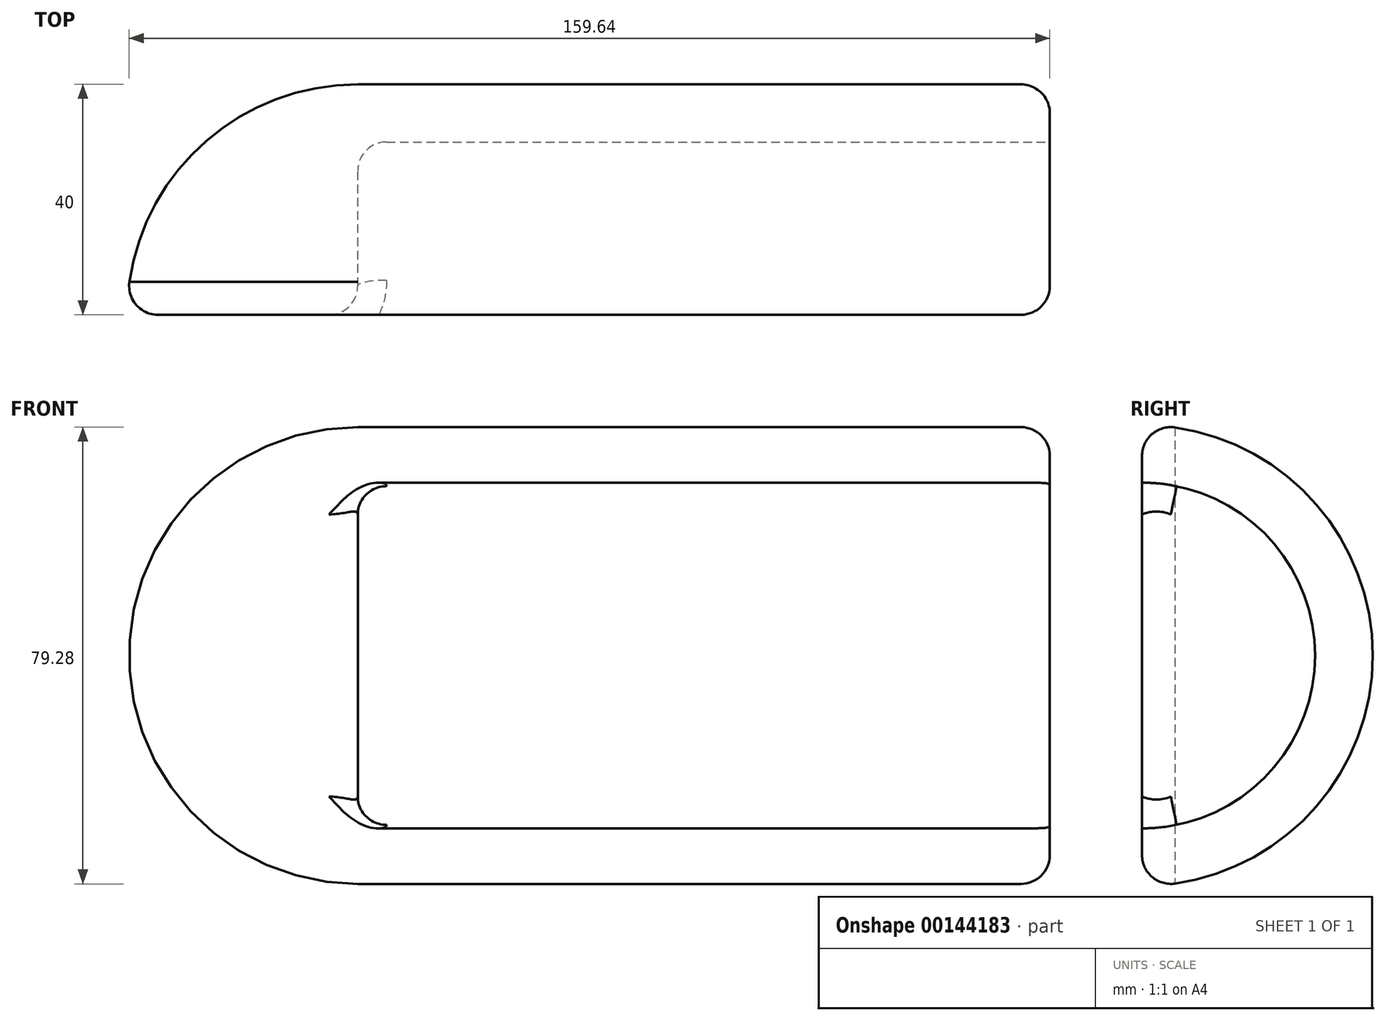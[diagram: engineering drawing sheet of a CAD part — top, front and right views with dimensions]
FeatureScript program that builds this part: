
annotation { "Feature Type Name" : "Feature", "Feature Type Description" : "" }
export const myFeature = defineFeature(function(context is Context, id is Id, definition is map)
    precondition{}
    {
        {
            var Q0;
            Q0=qCreatedBy(makeId("Front.planeOp"),FACE);
            var sketch = newSketch(context, id + "F0", { "sketchPlane" : qUnion([Q0])});
            skLineSegment(sketch, "E0", {"start": v(0, 40) * mm, "end": v(-120, 40) * mm});
            skLineSegment(sketch, "E1", {"start": v(0, 0) * mm, "end": v(-130.73, 0) * mm, "construction": true});
            skArc(sketch, "E2", {"start": v(-120, 40) * mm, "mid": v(-148.28, 28.28) * mm, "end": v(-160, 0) * mm});
            skLineSegment(sketch, "E3", {"start": v(-160, 0) * mm, "end": v(0, 0) * mm});
            skLineSegment(sketch, "E4", {"start": v(0, 40) * mm, "end": v(0, 0) * mm});
            skSolve(sketch);
        }
        {
            var Q0;
            Q0=makeQuery(id+"F0.imprint","IMPRINT",FACE,{"disambiguationData":[TD([[makeQuery(id+"F0.imprint","IMPRINT",EDGE,{"derivedFrom":sQuery(id+"F0.wireOp",EDGE,"E0")}),1.0]])]});
            var Q1;
            Q1=sQuery(id+"F0.wireOp",EDGE,"E1");
            revolve(context, id + "F1", {"entities" : qUnion([Q0]), "axis" : qUnion([Q1]), "revolveType" : RevolveType.FULL});
        }
        {
            var Q0;
            Q0=makeQuery(id+"F1.opRevolve","SWEPT_FACE",FACE,{"disambiguationData":[OSD([sQuery(id+"F0.wireOp",EDGE,"E4")])]});
            var sketch = newSketch(context, id + "F2", { "sketchPlane" : qUnion([Q0])});
            skCircle(sketch, "E5", {"center": v(0, 0) * mm, "radius": 30 * mm});
            skSolve(sketch);
        }
        {
            var Q0;
            Q0=makeQuery(id+"F2.imprint","IMPRINT",FACE,{"disambiguationData":[TD([[makeQuery(id+"F2.imprint","IMPRINT",EDGE,{"derivedFrom":sQuery(id+"F2.wireOp",EDGE,"E5")}),1.0]])]});
            extrude(context, id + "F3", {"entities" : qUnion([Q0]), "operationType" : NewBodyOperationType.REMOVE, "oppositeDirection" : true, "depth" : 120 * mm});
        }
        {
            var Q0;
            Q0=qCreatedBy(makeId("Top.planeOp"),FACE);
            var sketch = newSketch(context, id + "F4", { "sketchPlane" : qUnion([Q0])});
            skLineSegment(sketch, "E6", {"start": v(0, 0) * mm, "end": v(-176.6, 0) * mm});
            skLineSegment(sketch, "E7", {"start": v(-176.6, 0) * mm, "end": v(-176.6, -76.2) * mm});
            skLineSegment(sketch, "E8", {"start": v(-176.6, -76.2) * mm, "end": v(48.55, -72.12) * mm});
            skLineSegment(sketch, "E9", {"start": v(48.55, -72.12) * mm, "end": v(47.24, 0) * mm});
            skLineSegment(sketch, "E10", {"start": v(47.24, 0) * mm, "end": v(0, 0) * mm});
            skSolve(sketch);
        }
        {
            var Q0;
            Q0=makeQuery(id+"F4.imprint","IMPRINT",FACE,{"disambiguationData":[TD([[makeQuery(id+"F4.imprint","IMPRINT",EDGE,{"derivedFrom":sQuery(id+"F4.wireOp",EDGE,"E6")}),1.0]])]});
            extrude(context, id + "F5", {"entities" : qUnion([Q0]), "operationType" : NewBodyOperationType.REMOVE, "endBound" : BoundingType.SYMMETRIC, "oppositeDirection" : true, "depth" : 100 * mm});
        }
        {
            var Q0;
            Q0=makeQuery(id+"F3.boolean.opBoolean","COPY",EDGE,{"derivedFrom":makeQuery(id+"F3.opExtrude","CAP_EDGE",EDGE,{"disambiguationData":[OSD([sQuery(id+"F2.wireOp",EDGE,"E5")])],"isStart":true})});
            var Q1;
            Q1=makeQuery(id+"F1.opRevolve","SWEPT_EDGE",EDGE,{"disambiguationData":[OSD([sQuery(id+"F0.wireOp",EDGE,"E0"),sQuery(id+"F0.wireOp",EDGE,"E4")])]});
            var Q2;
            Q2=makeQuery(id+"F5.boolean.opBoolean","INTERSECT",EDGE,{"derivedFrom":[makeQuery(id+"F3.boolean.opBoolean","COPY",FACE,{"derivedFrom":makeQuery(id+"F3.opExtrude","CAP_FACE",FACE,{"disambiguationData":[OSD([sQuery(id+"F2.wireOp",EDGE,"E5")])],"isStart":false})}),makeQuery(id+"F5.opExtrude","SWEPT_FACE",FACE,{"disambiguationData":[OSD([sQuery(id+"F4.wireOp",EDGE,"E6"),sQuery(id+"F4.wireOp",EDGE,"E10")])]})]});
            fillet(context, id + "F6", {"entities" : qUnion([Q0, Q1, Q2]), "radius" : 5 * mm, "tangentPropagation" : true, "allowEdgeOverflow" : false});
        }
        {
            var Q0;
            Q0=makeQuery(id+"F3.boolean.opBoolean","COPY",EDGE,{"derivedFrom":makeQuery(id+"F3.opExtrude","CAP_EDGE",EDGE,{"disambiguationData":[OSD([sQuery(id+"F2.wireOp",EDGE,"E5")])],"isStart":false})});
            var Q1;
            Q1=makeQuery(id+"F5.boolean.opBoolean","INTERSECT",EDGE,{"disambiguationData":[OD(1.0)],"derivedFrom":[makeQuery(id+"F1.opRevolve","SWEPT_FACE",FACE,{"disambiguationData":[OSD([sQuery(id+"F0.wireOp",EDGE,"E0")])]}),makeQuery(id+"F5.opExtrude","SWEPT_FACE",FACE,{"disambiguationData":[OSD([sQuery(id+"F4.wireOp",EDGE,"E6"),sQuery(id+"F4.wireOp",EDGE,"E10")])]})]});
            fillet(context, id + "F7", {"entities" : qUnion([Q0, Q1]), "radius" : 5 * mm, "tangentPropagation" : true, "allowEdgeOverflow" : false});
        }
    });
